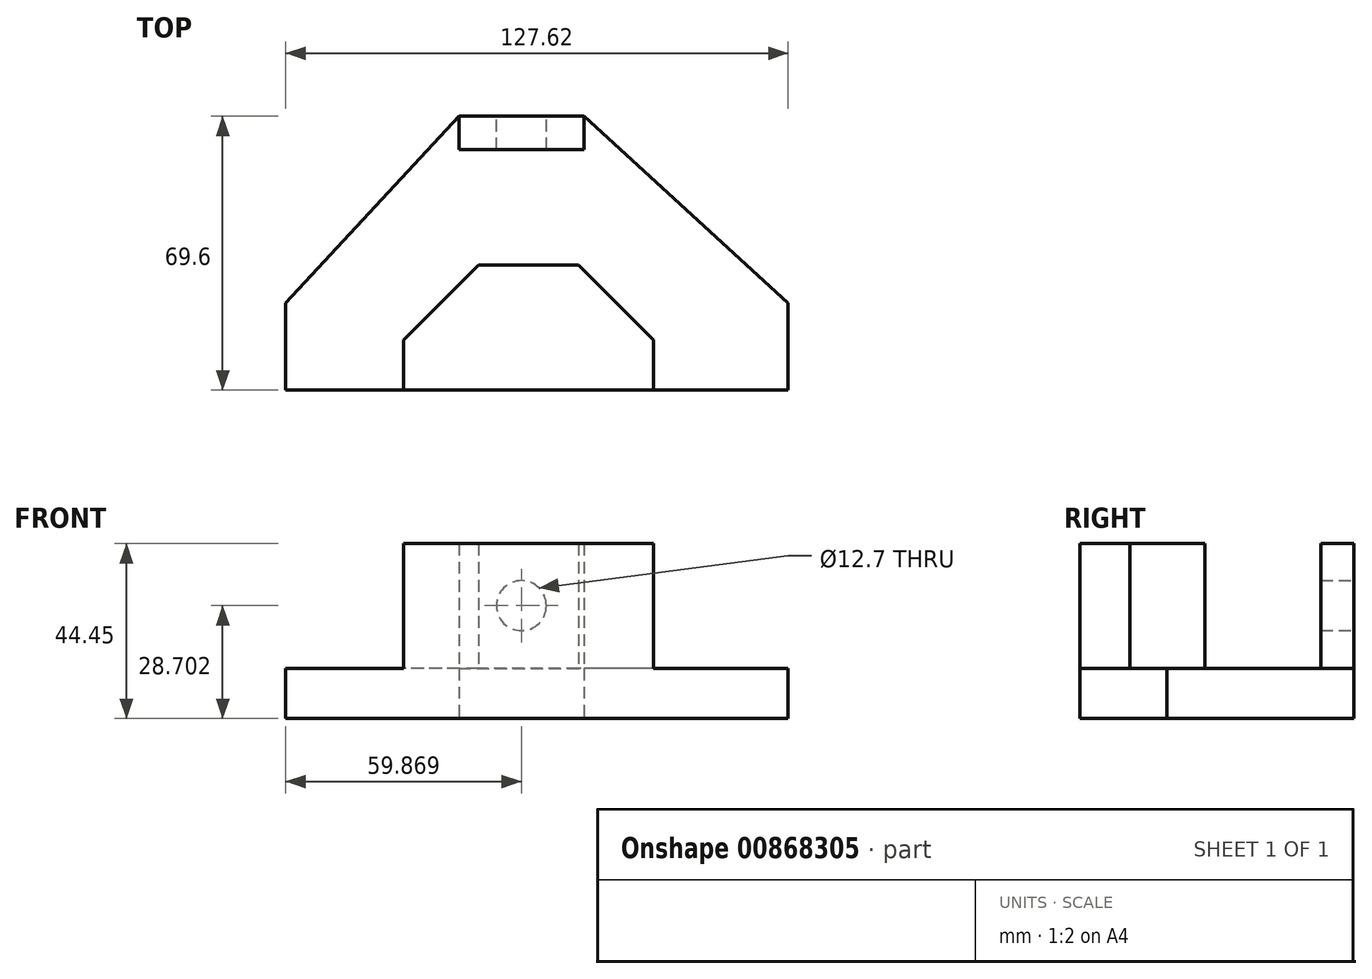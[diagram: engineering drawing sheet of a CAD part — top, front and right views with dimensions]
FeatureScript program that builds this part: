
annotation { "Feature Type Name" : "Feature", "Feature Type Description" : "" }
export const myFeature = defineFeature(function(context is Context, id is Id, definition is map)
    precondition{}
    {
        {
            var Q0;
            Q0=qCreatedBy(makeId("Top.planeOp"),FACE);
            var sketch = newSketch(context, id + "F0", { "sketchPlane" : qUnion([Q0])});
            skLineSegment(sketch, "E0", {"start": v(-61.94, 0) * mm, "end": v(65.06, 0) * mm});
            skLineSegment(sketch, "E1", {"start": v(65.06, 0) * mm, "end": v(65.06, 22.1) * mm});
            skLineSegment(sketch, "E2", {"start": v(65.06, 22.1) * mm, "end": v(13.18, 69.6) * mm});
            skLineSegment(sketch, "E3", {"start": v(13.18, 69.6) * mm, "end": v(-18.57, 69.6) * mm});
            skLineSegment(sketch, "E4", {"start": v(-18.57, 69.6) * mm, "end": v(-62.56, 22.1) * mm});
            skLineSegment(sketch, "E5", {"start": v(-62.56, 22.1) * mm, "end": v(-62.56, 0) * mm});
            skLineSegment(sketch, "E6", {"start": v(-62.56, 0) * mm, "end": v(-61.94, 0) * mm});
            skLineSegment(sketch, "E7", {"start": v(-18.57, 69.6) * mm, "end": v(-18.57, 61.17) * mm});
            skLineSegment(sketch, "E8", {"start": v(-18.57, 61.17) * mm, "end": v(13.18, 61.17) * mm});
            skLineSegment(sketch, "E9", {"start": v(13.18, 61.17) * mm, "end": v(13.18, 69.6) * mm});
            skLineSegment(sketch, "E10", {"start": v(-32.67, 0) * mm, "end": v(30.83, 0) * mm});
            skLineSegment(sketch, "E11", {"start": v(30.83, 0) * mm, "end": v(30.83, 12.7) * mm});
            skLineSegment(sketch, "E12", {"start": v(30.83, 12.7) * mm, "end": v(11.78, 31.75) * mm});
            skLineSegment(sketch, "E13", {"start": v(11.78, 31.75) * mm, "end": v(-13.62, 31.75) * mm});
            skLineSegment(sketch, "E14", {"start": v(-13.62, 31.75) * mm, "end": v(-32.67, 12.7) * mm});
            skLineSegment(sketch, "E15", {"start": v(-32.67, 12.7) * mm, "end": v(-32.67, 0) * mm});
            skSolve(sketch);
        }
        {
            var Q0;
            {var subQ1=sQuery(id+"F0.wireOp",EDGE,"E1");Q0=makeQuery(id+"F0.imprint","IMPRINT",FACE,{"disambiguationData":[TD([[makeQuery(id+"F0.imprint","IMPRINT",EDGE,{"derivedFrom":subQ1}),1.0]])]});}
            extrude(context, id + "F1", {"entities" : qUnion([Q0]), "depth" : 12.7 * mm, "offsetDistance" : 25.4 * mm});
        }
        {
            var Q0;
            {var subQ0=sQuery(id+"F0.wireOp",EDGE,"E11");Q0=makeQuery(id+"F0.imprint","IMPRINT",FACE,{"disambiguationData":[TD([[makeQuery(id+"F0.imprint","IMPRINT",EDGE,{"derivedFrom":subQ0}),1.0]])]});}
            extrude(context, id + "F2", {"entities" : qUnion([Q0]), "operationType" : NewBodyOperationType.ADD, "depth" : 44.45 * mm, "offsetDistance" : 25.4 * mm});
        }
        {
            var Q0;
            Q0=makeQuery(id+"F0.imprint","IMPRINT",FACE,{"disambiguationData":[TD([[makeQuery(id+"F0.imprint","IMPRINT",EDGE,{"derivedFrom":sQuery(id+"F0.wireOp",EDGE,"E3")}),1.0]])]});
            var Q1;
            Q1=sQuery(id+"F0.wireOp",EDGE,"E14");
            var Q2;
            Q2=sQuery(id+"F0.wireOp",EDGE,"E15");
            var Q3;
            Q3=sQuery(id+"F0.wireOp",EDGE,"E13");
            var Q4;
            Q4=sQuery(id+"F0.wireOp",EDGE,"E12");
            var Q5;
            Q5=sQuery(id+"F0.wireOp",EDGE,"E11");
            var Q6;
            Q6=sQuery(id+"F0.wireOp",EDGE,"E10");
            extrude(context, id + "F3", {"entities" : qUnion([Q0]), "operationType" : NewBodyOperationType.ADD, "surfaceEntities" : qUnion([Q1, Q2, Q3, Q4, Q5, Q6]), "depth" : 44.45 * mm, "offsetDistance" : 25.4 * mm});
        }
        {
            var Q0;
            Q0=makeQuery(id+"F3.opExtrude","SWEPT_FACE",FACE,{"disambiguationData":[OSD([sQuery(id+"F0.wireOp",EDGE,"E3")])]});
            var sketch = newSketch(context, id + "F4", { "sketchPlane" : qUnion([Q0])});
            skCircle(sketch, "E16", {"center": v(2.7, 28.7) * mm, "radius": 6.35 * mm});
            skSolve(sketch);
        }
        {
            var Q0;
            Q0=makeQuery(id+"F4.imprint","IMPRINT",FACE,{"disambiguationData":[TD([[makeQuery(id+"F4.imprint","IMPRINT",EDGE,{"derivedFrom":sQuery(id+"F4.wireOp",EDGE,"E16")}),1.0]])]});
            extrude(context, id + "F5", {"entities" : qUnion([Q0]), "operationType" : NewBodyOperationType.REMOVE, "oppositeDirection" : true, "depth" : 14.22 * mm, "offsetDistance" : 25.4 * mm});
        }
    });
